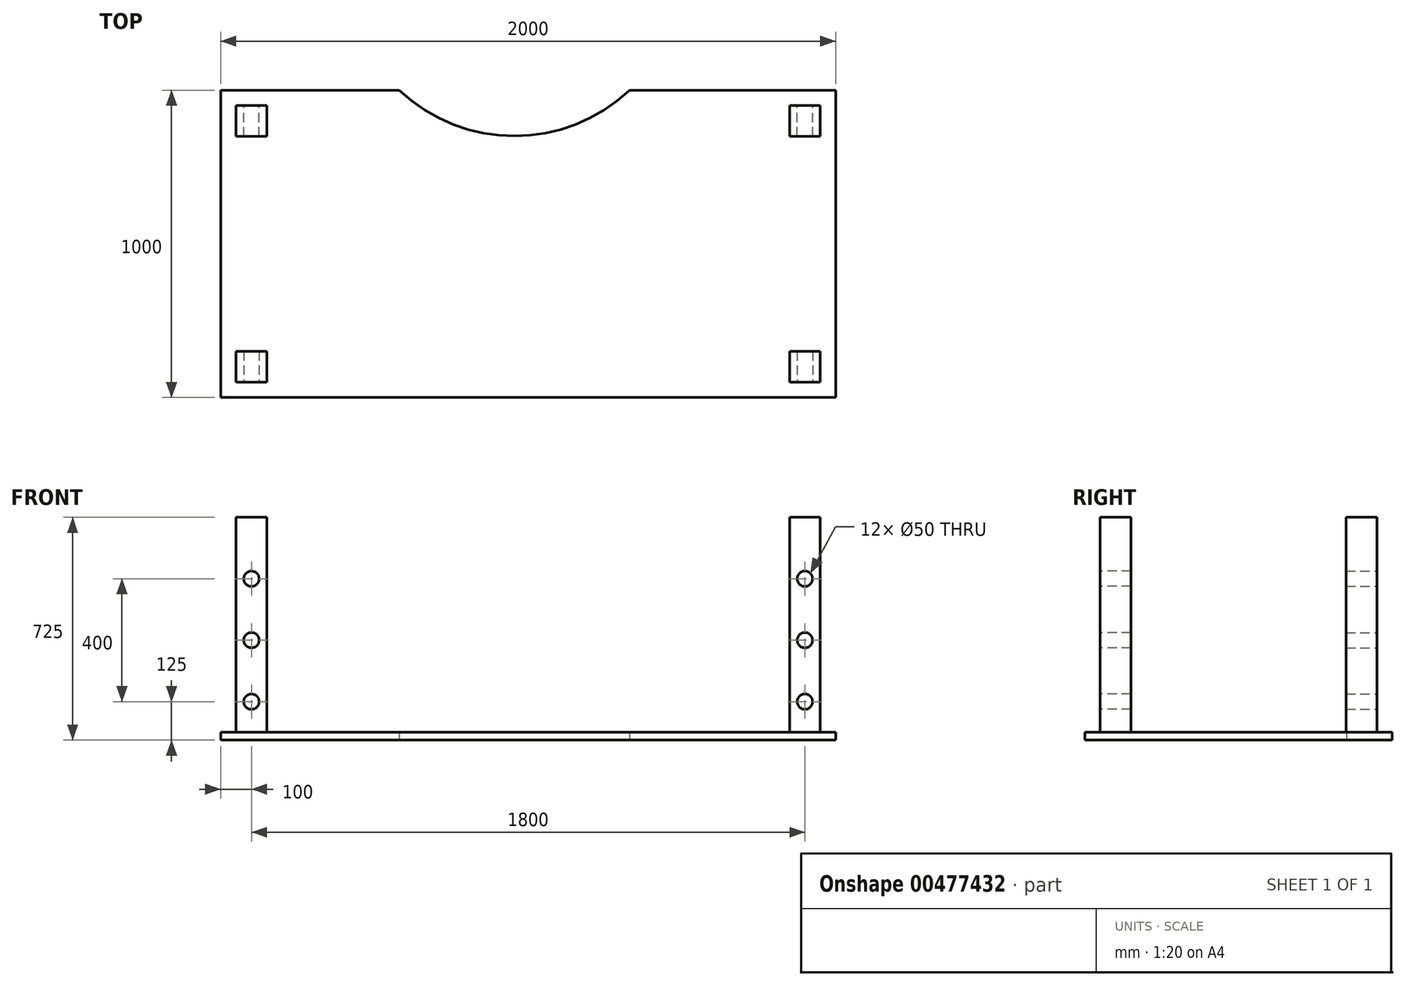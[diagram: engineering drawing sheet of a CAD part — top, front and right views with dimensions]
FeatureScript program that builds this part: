
annotation { "Feature Type Name" : "Feature", "Feature Type Description" : "" }
export const myFeature = defineFeature(function(context is Context, id is Id, definition is map)
    precondition{}
    {
        {
            var Q0;
            Q0=qCreatedBy(makeId("Top.planeOp"),FACE);
            var sketch = newSketch(context, id + "F0", { "sketchPlane" : qUnion([Q0])});
            skLineSegment(sketch, "E0.bottom", {"start": v(-992.2, 418.59) * mm, "end": v(1007.8, 418.59) * mm});
            skLineSegment(sketch, "E0.top", {"start": v(-992.2, -581.41) * mm, "end": v(1007.8, -581.41) * mm});
            skLineSegment(sketch, "E0.left", {"start": v(-992.2, 418.59) * mm, "end": v(-992.2, -581.41) * mm});
            skLineSegment(sketch, "E0.right", {"start": v(1007.8, 418.59) * mm, "end": v(1007.8, -581.41) * mm});
            skSolve(sketch);
        }
        {
            var Q0;
            Q0=makeQuery(id+"F0.imprint","IMPRINT",FACE,{"disambiguationData":[TD([[makeQuery(id+"F0.imprint","IMPRINT",EDGE,{"derivedFrom":sQuery(id+"F0.wireOp",EDGE,"E0.bottom")}),-1.0]])]});
            extrude(context, id + "F1", {"entities" : qUnion([Q0]), "depth" : 25 * mm});
        }
        {
            var Q0;
            Q0=makeQuery(id+"F1.opExtrude","CAP_FACE",FACE,{"disambiguationData":[OSD([sQuery(id+"F0.wireOp",EDGE,"E0.bottom"),sQuery(id+"F0.wireOp",EDGE,"E0.top"),sQuery(id+"F0.wireOp",EDGE,"E0.left"),sQuery(id+"F0.wireOp",EDGE,"E0.right")])],"isStart":false});
            var sketch = newSketch(context, id + "F2", { "sketchPlane" : qUnion([Q0])});
            skLineSegment(sketch, "E1.bottom", {"start": v(-942.2, 368.59) * mm, "end": v(-842.2, 368.59) * mm});
            skLineSegment(sketch, "E1.top", {"start": v(-942.2, 268.59) * mm, "end": v(-842.2, 268.59) * mm});
            skLineSegment(sketch, "E1.left", {"start": v(-942.2, 368.59) * mm, "end": v(-942.2, 268.59) * mm});
            skLineSegment(sketch, "E1.right", {"start": v(-842.2, 368.59) * mm, "end": v(-842.2, 268.59) * mm});
            skSolve(sketch);
        }
        {
            var Q0;
            Q0=qSketchRegion(id+"F2",true);
            extrude(context, id + "F3", {"entities" : qUnion([Q0]), "operationType" : NewBodyOperationType.ADD, "depth" : 700 * mm});
        }
        {
            var Q0;
            Q0=makeQuery(id+"F3.opExtrude","SWEPT_FACE",FACE,{"disambiguationData":[OSD([sQuery(id+"F2.wireOp",EDGE,"E1.bottom")])]});
            var sketch = newSketch(context, id + "F4", { "sketchPlane" : qUnion([Q0])});
            skCircle(sketch, "E2", {"center": v(892.2, 125) * mm, "radius": 25 * mm});
            skPoint(sketch, "E3.centerSnap0", {"position": v(892.2, 25) * mm});
            skCircle(sketch, "E4", {"center": v(892.2, 325) * mm, "radius": 25 * mm});
            skCircle(sketch, "E5", {"center": v(892.2, 525) * mm, "radius": 25 * mm});
            skSolve(sketch);
        }
        {
            var Q0;
            Q0=qSketchRegion(id+"F4",true);
            extrude(context, id + "F5", {"entities" : qUnion([Q0]), "operationType" : NewBodyOperationType.REMOVE, "oppositeDirection" : true, "depth" : 100 * mm});
        }
        {
            var Q0;
            Q0=makeQuery(id+"F1.opExtrude","CAP_FACE",FACE,{"disambiguationData":[OSD([sQuery(id+"F0.wireOp",EDGE,"E0.bottom"),sQuery(id+"F0.wireOp",EDGE,"E0.top"),sQuery(id+"F0.wireOp",EDGE,"E0.left"),sQuery(id+"F0.wireOp",EDGE,"E0.right")])],"isStart":false});
            var sketch = newSketch(context, id + "F6", { "sketchPlane" : qUnion([Q0])});
            skLineSegment(sketch, "E6.bottom", {"start": v(857.8, 368.59) * mm, "end": v(957.8, 368.59) * mm});
            skLineSegment(sketch, "E6.top", {"start": v(857.8, 268.59) * mm, "end": v(957.8, 268.59) * mm});
            skLineSegment(sketch, "E6.left", {"start": v(857.8, 368.59) * mm, "end": v(857.8, 268.59) * mm});
            skLineSegment(sketch, "E6.right", {"start": v(957.8, 368.59) * mm, "end": v(957.8, 268.59) * mm});
            skSolve(sketch);
        }
        {
            var Q0;
            Q0=qSketchRegion(id+"F6",true);
            extrude(context, id + "F7", {"entities" : qUnion([Q0]), "operationType" : NewBodyOperationType.ADD, "depth" : 700 * mm});
        }
        {
            var Q0;
            Q0=makeQuery(id+"F7.opExtrude","SWEPT_FACE",FACE,{"disambiguationData":[OSD([sQuery(id+"F6.wireOp",EDGE,"E6.bottom")])]});
            var sketch = newSketch(context, id + "F8", { "sketchPlane" : qUnion([Q0])});
            skCircle(sketch, "E7", {"center": v(-907.8, 125) * mm, "radius": 25 * mm});
            skCircle(sketch, "E8", {"center": v(-907.8, 325) * mm, "radius": 25 * mm});
            skCircle(sketch, "E9", {"center": v(-907.8, 525) * mm, "radius": 25 * mm});
            skSolve(sketch);
        }
        {
            var Q0;
            Q0=qSketchRegion(id+"F8",true);
            extrude(context, id + "F9", {"entities" : qUnion([Q0]), "operationType" : NewBodyOperationType.REMOVE, "oppositeDirection" : true, "depth" : 100 * mm});
        }
        {
            var Q0;
            Q0=makeQuery(id+"F1.opExtrude","CAP_FACE",FACE,{"disambiguationData":[OSD([sQuery(id+"F0.wireOp",EDGE,"E0.bottom"),sQuery(id+"F0.wireOp",EDGE,"E0.top"),sQuery(id+"F0.wireOp",EDGE,"E0.left"),sQuery(id+"F0.wireOp",EDGE,"E0.right")])],"isStart":false});
            var sketch = newSketch(context, id + "F10", { "sketchPlane" : qUnion([Q0])});
            skLineSegment(sketch, "E10.bottom", {"start": v(-942.2, -431.41) * mm, "end": v(-842.2, -431.41) * mm});
            skLineSegment(sketch, "E10.top", {"start": v(-942.2, -531.41) * mm, "end": v(-842.2, -531.41) * mm});
            skLineSegment(sketch, "E10.left", {"start": v(-942.2, -431.41) * mm, "end": v(-942.2, -531.41) * mm});
            skLineSegment(sketch, "E10.right", {"start": v(-842.2, -431.41) * mm, "end": v(-842.2, -531.41) * mm});
            skSolve(sketch);
        }
        {
            var Q0;
            Q0=qSketchRegion(id+"F10",true);
            extrude(context, id + "F11", {"entities" : qUnion([Q0]), "operationType" : NewBodyOperationType.ADD, "depth" : 700 * mm});
        }
        {
            var Q0;
            Q0=makeQuery(id+"F11.opExtrude","SWEPT_FACE",FACE,{"disambiguationData":[OSD([sQuery(id+"F10.wireOp",EDGE,"E10.top")])]});
            var sketch = newSketch(context, id + "F12", { "sketchPlane" : qUnion([Q0])});
            skCircle(sketch, "E11", {"center": v(-892.2, 525) * mm, "radius": 25 * mm});
            skCircle(sketch, "E12", {"center": v(-892.2, 325) * mm, "radius": 25 * mm});
            skCircle(sketch, "E13", {"center": v(-892.2, 125) * mm, "radius": 25 * mm});
            skSolve(sketch);
        }
        {
            var Q0;
            Q0=qSketchRegion(id+"F12",true);
            extrude(context, id + "F13", {"entities" : qUnion([Q0]), "operationType" : NewBodyOperationType.REMOVE, "oppositeDirection" : true, "depth" : 100 * mm});
        }
        {
            var Q0;
            Q0=makeQuery(id+"F1.opExtrude","CAP_FACE",FACE,{"disambiguationData":[OSD([sQuery(id+"F0.wireOp",EDGE,"E0.bottom"),sQuery(id+"F0.wireOp",EDGE,"E0.top"),sQuery(id+"F0.wireOp",EDGE,"E0.left"),sQuery(id+"F0.wireOp",EDGE,"E0.right")])],"isStart":false});
            var sketch = newSketch(context, id + "F14", { "sketchPlane" : qUnion([Q0])});
            skLineSegment(sketch, "E14.bottom", {"start": v(857.8, -431.41) * mm, "end": v(957.8, -431.41) * mm});
            skLineSegment(sketch, "E14.top", {"start": v(857.8, -531.41) * mm, "end": v(957.8, -531.41) * mm});
            skLineSegment(sketch, "E14.left", {"start": v(857.8, -431.41) * mm, "end": v(857.8, -531.41) * mm});
            skLineSegment(sketch, "E14.right", {"start": v(957.8, -431.41) * mm, "end": v(957.8, -531.41) * mm});
            skSolve(sketch);
        }
        {
            var Q0;
            Q0=qSketchRegion(id+"F14",true);
            extrude(context, id + "F15", {"entities" : qUnion([Q0]), "operationType" : NewBodyOperationType.ADD, "depth" : 700 * mm});
        }
        {
            var Q0;
            Q0=makeQuery(id+"F15.opExtrude","SWEPT_FACE",FACE,{"disambiguationData":[OSD([sQuery(id+"F14.wireOp",EDGE,"E14.top")])]});
            var sketch = newSketch(context, id + "F16", { "sketchPlane" : qUnion([Q0])});
            skCircle(sketch, "E15", {"center": v(907.8, 525) * mm, "radius": 25 * mm});
            skCircle(sketch, "E16", {"center": v(907.8, 325) * mm, "radius": 25 * mm});
            skCircle(sketch, "E17", {"center": v(907.8, 125) * mm, "radius": 25 * mm});
            skSolve(sketch);
        }
        {
            var Q0;
            Q0=qSketchRegion(id+"F16",true);
            extrude(context, id + "F17", {"entities" : qUnion([Q0]), "operationType" : NewBodyOperationType.REMOVE, "oppositeDirection" : true, "depth" : 100 * mm});
        }
        {
            var Q0;
            Q0=makeQuery(id+"F1.opExtrude","CAP_FACE",FACE,{"disambiguationData":[OSD([sQuery(id+"F0.wireOp",EDGE,"E0.bottom"),sQuery(id+"F0.wireOp",EDGE,"E0.top"),sQuery(id+"F0.wireOp",EDGE,"E0.left"),sQuery(id+"F0.wireOp",EDGE,"E0.right")])],"isStart":true});
            var sketch = newSketch(context, id + "F18", { "sketchPlane" : qUnion([Q0])});
            skArc(sketch, "E18", {"start": v(337.69, -418.59) * mm, "mid": v(-36.73, -269.43) * mm, "end": v(-411.14, -418.59) * mm});
            skSolve(sketch);
        }
        {
            var Q0;
            {var subQ0=sQuery(id+"F18.wireOp",EDGE,"E18");Q0=makeQuery(id+"F18.imprint","IMPRINT",FACE,{"disambiguationData":[TD([[makeQuery(id+"F18.imprint","IMPRINT",EDGE,{"derivedFrom":subQ0}),1.0]])]});}
            var Q1;
            Q1=sQuery(id+"F18.wireOp",EDGE,"E18");
            extrude(context, id + "F19", {"entities" : qUnion([Q0]), "operationType" : NewBodyOperationType.REMOVE, "surfaceEntities" : qUnion([Q1]), "oppositeDirection" : true, "depth" : 25 * mm});
        }
    });
